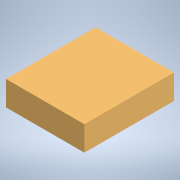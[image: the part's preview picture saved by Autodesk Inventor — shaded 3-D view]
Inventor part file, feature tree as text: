
AUTODESK INVENTOR PART (.ipt)
format: ipt  version: 2022.3 (Build 263350000, 350)  size: 99,328 bytes
history: native  units: in
note: dims shown in document units (in); Inventor stores cm internally (conversion verified against a paired STEP export)
features: extrude x1, sketch x1
ambient origin geometry x8: Origin, YZ Plane, XZ Plane, XY Plane, X Axis, Y Axis, Z Axis, Center Point
bodies: Solid1 (feature_tree)
feature tree (2):
  extrude  "Extrusion1"  Depth=3.5in
  sketch  "Sketch1"  dims[d0=4.0in d1=3.5in d2=1.1in d3=0.0in]
